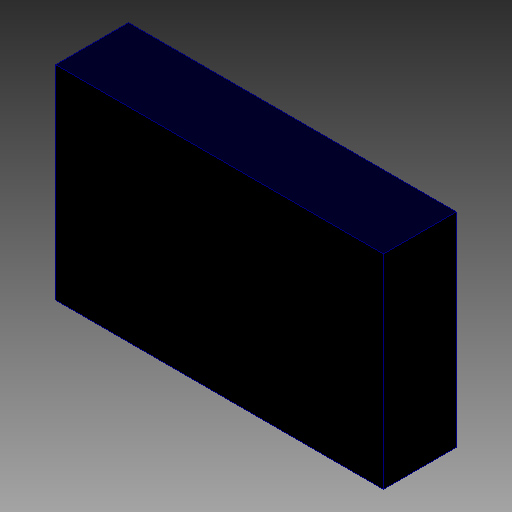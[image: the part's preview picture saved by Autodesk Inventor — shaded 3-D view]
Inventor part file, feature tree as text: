
AUTODESK INVENTOR PART (.ipt)
format: ipt  version: 2018 (Build 220112000, 112)  size: 80,384 bytes
history: native  units: in
note: dims shown in document units (in); Inventor stores cm internally (conversion verified against a paired STEP export)
features: other x1, extrude x1
ambient origin geometry x8: Origin, YZ Plane, XZ Plane, XY Plane, X Axis, Y Axis, Z Axis, Center Point
bodies: Solid1 (feature_tree)
feature tree (2):
  other  "MURATA-FILTER_CSTCR, CSTCR6M00G15L99_97"
  extrude  "Extrusion1"  Depth=0.0394in TaperAngle=0.0deg
